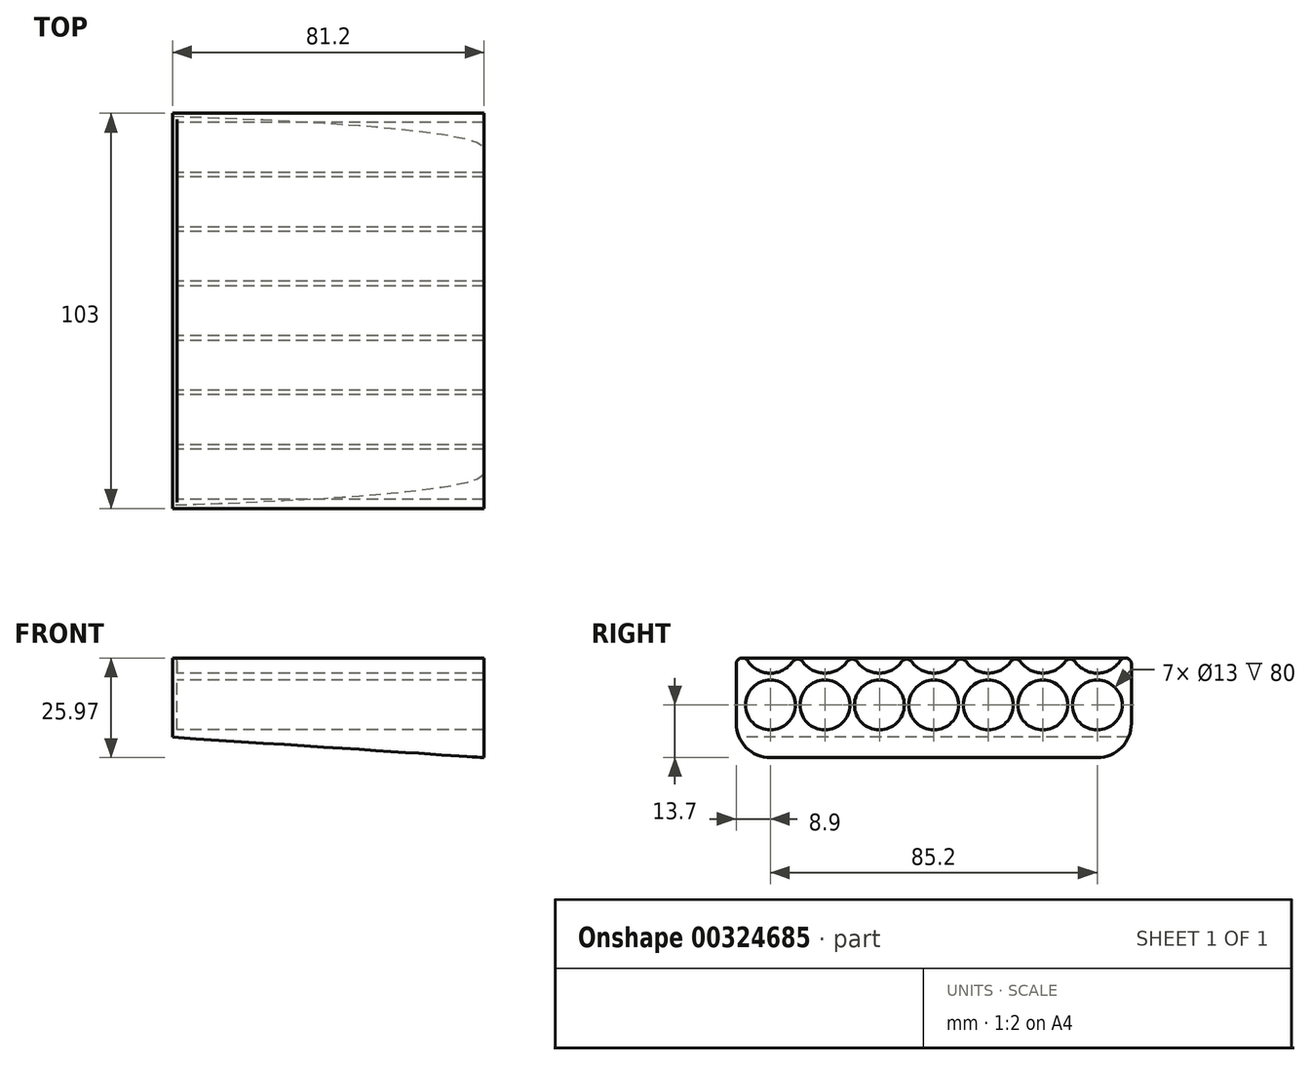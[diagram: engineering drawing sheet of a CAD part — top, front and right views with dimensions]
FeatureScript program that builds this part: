
annotation { "Feature Type Name" : "Feature", "Feature Type Description" : "" }
export const myFeature = defineFeature(function(context is Context, id is Id, definition is map)
    precondition{}
    {
        {
            var Q0;
            Q0=qCreatedBy(makeId("Right.planeOp"),FACE);
            var sketch = newSketch(context, id + "F0", { "sketchPlane" : qUnion([Q0])});
            skCircle(sketch, "E0", {"center": v(0, 0) * mm, "radius": 6.5 * mm});
            skCircle(sketch, "E1.1.0.0", {"center": v(14.2, 0) * mm, "radius": 6.5 * mm});
            skCircle(sketch, "E1.2.0.0", {"center": v(28.4, 0) * mm, "radius": 6.5 * mm});
            skCircle(sketch, "E1.3.0.0", {"center": v(42.6, 0) * mm, "radius": 6.5 * mm});
            skCircle(sketch, "E1.4.0.0", {"center": v(56.8, 0) * mm, "radius": 6.5 * mm});
            skCircle(sketch, "E1.5.0.0", {"center": v(71, 0) * mm, "radius": 6.5 * mm});
            skCircle(sketch, "E1.6.0.0", {"center": v(85.2, 0) * mm, "radius": 6.5 * mm});
            skLineSegment(sketch, "E1.direction1", {"start": v(0, 0) * mm, "end": v(14.2, 0) * mm, "construction": true});
            skLineSegment(sketch, "E2.top", {"start": v(0, -13.7) * mm, "end": v(85.2, -13.7) * mm});
            skLineSegment(sketch, "E2.left", {"start": v(-8.9, 11) * mm, "end": v(-8.9, -4.8) * mm});
            skLineSegment(sketch, "E2.right", {"start": v(94.1, 11) * mm, "end": v(94.1, -4.8) * mm});
            skArc(sketch, "E3", {"start": v(-7.05, 14.58) * mm, "mid": v(0.4, 8.31) * mm, "end": v(7.1, 15.4) * mm});
            skArc(sketch, "E4.1.0.0", {"start": v(7.1, 15.4) * mm, "mid": v(14.2, 8.3) * mm, "end": v(21.3, 15.4) * mm});
            skArc(sketch, "E4.2.0.0", {"start": v(21.3, 15.4) * mm, "mid": v(28.4, 8.3) * mm, "end": v(35.5, 15.4) * mm});
            skArc(sketch, "E4.3.0.0", {"start": v(35.5, 15.4) * mm, "mid": v(42.6, 8.3) * mm, "end": v(49.7, 15.4) * mm});
            skArc(sketch, "E4.4.0.0", {"start": v(49.7, 15.4) * mm, "mid": v(56.8, 8.3) * mm, "end": v(63.9, 15.4) * mm});
            skArc(sketch, "E4.5.0.0", {"start": v(63.9, 15.4) * mm, "mid": v(71, 8.3) * mm, "end": v(78.1, 15.4) * mm});
            skArc(sketch, "E4.6.0.0", {"start": v(78.1, 15.4) * mm, "mid": v(84.8, 8.31) * mm, "end": v(92.25, 14.58) * mm});
            skPoint(sketch, "E5.visualSharp", {"position": v(-8.9, -13.7) * mm});
            skArc(sketch, "E5.filletArc", {"start": v(-8.9, -4.8) * mm, "mid": v(-6.3, -11.1) * mm, "end": v(0, -13.7) * mm});
            skPoint(sketch, "E6.visualSharp", {"position": v(94.1, -13.7) * mm});
            skArc(sketch, "E6.filletArc", {"start": v(85.2, -13.7) * mm, "mid": v(91.5, -11.1) * mm, "end": v(94.1, -4.8) * mm});
            skPoint(sketch, "E7.visualSharp", {"position": v(-8.9, 15.4) * mm});
            skArc(sketch, "E7.filletArc", {"start": v(-7.05, 14.58) * mm, "mid": v(-8.41, 13.02) * mm, "end": v(-8.9, 11) * mm});
            skPoint(sketch, "E8.visualSharp", {"position": v(94.1, 15.4) * mm});
            skArc(sketch, "E8.filletArc", {"start": v(94.1, 11) * mm, "mid": v(93.61, 13.02) * mm, "end": v(92.25, 14.58) * mm});
            skSolve(sketch);
        }
        {
            var Q0;
            Q0 = qSketchRegion(id + "F0", true);
            extrude(context, id + "F1", {"entities" : qUnion([Q0]), "depth" : 80 * mm});
        }
        {
            var Q0;
            Q0=makeQuery(id+"F1.opExtrude","SWEPT_EDGE",EDGE,{"disambiguationData":[OSD([sQuery(id+"F0.wireOp",EDGE,"E4.5.0.0"),sQuery(id+"F0.wireOp",EDGE,"E4.6.0.0")])]});
            var Q1;
            Q1=makeQuery(id+"F1.opExtrude","SWEPT_EDGE",EDGE,{"disambiguationData":[OSD([sQuery(id+"F0.wireOp",EDGE,"E4.4.0.0"),sQuery(id+"F0.wireOp",EDGE,"E4.5.0.0")])]});
            var Q2;
            Q2=makeQuery(id+"F1.opExtrude","SWEPT_EDGE",EDGE,{"disambiguationData":[OSD([sQuery(id+"F0.wireOp",EDGE,"E4.3.0.0"),sQuery(id+"F0.wireOp",EDGE,"E4.4.0.0")])]});
            var Q3;
            Q3=makeQuery(id+"F1.opExtrude","SWEPT_EDGE",EDGE,{"disambiguationData":[OSD([sQuery(id+"F0.wireOp",EDGE,"E4.2.0.0"),sQuery(id+"F0.wireOp",EDGE,"E4.3.0.0")])]});
            var Q4;
            Q4=makeQuery(id+"F1.opExtrude","SWEPT_EDGE",EDGE,{"disambiguationData":[OSD([sQuery(id+"F0.wireOp",EDGE,"E4.1.0.0"),sQuery(id+"F0.wireOp",EDGE,"E4.2.0.0")])]});
            var Q5;
            Q5=makeQuery(id+"F1.opExtrude","SWEPT_EDGE",EDGE,{"disambiguationData":[OSD([sQuery(id+"F0.wireOp",EDGE,"E3"),sQuery(id+"F0.wireOp",EDGE,"E4.1.0.0")])]});
            var Q6;
            Q6=makeQuery(id+"F1.opExtrude","SWEPT_EDGE",EDGE,{"disambiguationData":[OSD([sQuery(id+"F0.wireOp",EDGE,"E4.6.0.0"),sQuery(id+"F0.wireOp",EDGE,"E8.filletArc")])]});
            var Q7;
            Q7=makeQuery(id+"F1.opExtrude","SWEPT_EDGE",EDGE,{"disambiguationData":[OSD([sQuery(id+"F0.wireOp",EDGE,"E3"),sQuery(id+"F0.wireOp",EDGE,"E7.filletArc")])]});
            fillet(context, id + "F2", {"entities" : qUnion([Q0, Q1, Q2, Q3, Q4, Q5, Q6, Q7]), "radius" : 1.6 * mm, "tangentPropagation" : true, "allowEdgeOverflow" : false});
        }
        {
            var Q0;
            Q0=makeQuery(id+"F1.opExtrude","CAP_FACE",FACE,{"disambiguationData":[OSD([sQuery(id+"F0.wireOp",EDGE,"E0"),sQuery(id+"F0.wireOp",EDGE,"E1.1.0.0"),sQuery(id+"F0.wireOp",EDGE,"E1.2.0.0"),sQuery(id+"F0.wireOp",EDGE,"E1.3.0.0"),sQuery(id+"F0.wireOp",EDGE,"E1.4.0.0"),sQuery(id+"F0.wireOp",EDGE,"E1.5.0.0"),sQuery(id+"F0.wireOp",EDGE,"E1.6.0.0"),sQuery(id+"F0.wireOp",EDGE,"E2.top"),sQuery(id+"F0.wireOp",EDGE,"E2.left"),sQuery(id+"F0.wireOp",EDGE,"E2.right"),sQuery(id+"F0.wireOp",EDGE,"E3"),sQuery(id+"F0.wireOp",EDGE,"E4.1.0.0"),sQuery(id+"F0.wireOp",EDGE,"E4.2.0.0"),sQuery(id+"F0.wireOp",EDGE,"E4.3.0.0"),sQuery(id+"F0.wireOp",EDGE,"E4.4.0.0"),sQuery(id+"F0.wireOp",EDGE,"E4.5.0.0"),sQuery(id+"F0.wireOp",EDGE,"E4.6.0.0"),sQuery(id+"F0.wireOp",EDGE,"E5.filletArc"),sQuery(id+"F0.wireOp",EDGE,"E6.filletArc"),sQuery(id+"F0.wireOp",EDGE,"E7.filletArc"),sQuery(id+"F0.wireOp",EDGE,"E8.filletArc")])],"isStart":true});
            var sketch = newSketch(context, id + "F3", { "sketchPlane" : qUnion([Q0])});
            skPoint(sketch, "E9.startSnap0", {"position": v(-92.95, 12.2) * mm});
            skPoint(sketch, "E9.endSnap0", {"position": v(-35.5, 11.97) * mm});
            skLineSegment(sketch, "E10.0", {"start": v(-94.1, 10.67) * mm, "end": v(-94.1, -4.8) * mm});
            skArc(sketch, "E10.1", {"start": v(-85.2, -13.7) * mm, "mid": v(-91.5, -11.1) * mm, "end": v(-94.1, -4.8) * mm});
            skLineSegment(sketch, "E10.2", {"start": v(0, -13.7) * mm, "end": v(-85.2, -13.7) * mm});
            skArc(sketch, "E10.3", {"start": v(8.9, -4.8) * mm, "mid": v(6.3, -11.1) * mm, "end": v(0, -13.7) * mm});
            skLineSegment(sketch, "E10.4", {"start": v(8.9, 10.67) * mm, "end": v(8.9, -4.8) * mm});
            skArc(sketch, "E10.5", {"start": v(8.9, 10.67) * mm, "mid": v(8.43, 11.8) * mm, "end": v(7.3, 12.27) * mm});
            skArc(sketch, "E10.6", {"start": v(-92.5, 12.27) * mm, "mid": v(-93.63, 11.8) * mm, "end": v(-94.1, 10.67) * mm});
            skLineSegment(sketch, "E11", {"start": v(-92.5, 12.27) * mm, "end": v(7.3, 12.27) * mm});
            skPoint(sketch, "E12.orphan", {"position": v(-91.16, 11.54) * mm});
            skPoint(sketch, "E13.orphan", {"position": v(5.96, 11.54) * mm});
            skSolve(sketch);
        }
        {
            var Q0;
            Q0 = qSketchRegion(id + "F3", true);
            extrude(context, id + "F4", {"entities" : qUnion([Q0]), "operationType" : NewBodyOperationType.ADD, "depth" : 1.2 * mm});
        }
        {
            var Q0;
            Q0=qCreatedBy(makeId("Front.planeOp"),FACE);
            var sketch = newSketch(context, id + "F5", { "sketchPlane" : qUnion([Q0])});
            skLineSegment(sketch, "E14", {"start": v(-1.2, -8.4) * mm, "end": v(79.8, -13.7) * mm});
            skLineSegment(sketch, "E15", {"start": v(79.8, -13.7) * mm, "end": v(79.8, -25.43) * mm});
            skLineSegment(sketch, "E16", {"start": v(79.8, -25.43) * mm, "end": v(-2.69, -26.33) * mm});
            skLineSegment(sketch, "E17", {"start": v(-2.69, -26.33) * mm, "end": v(-1.2, -8.4) * mm});
            skSolve(sketch);
        }
        {
            var Q0;
            Q0 = qSketchRegion(id + "F5", true);
            extrude(context, id + "F6", {"entities" : qUnion([Q0]), "operationType" : NewBodyOperationType.REMOVE, "endBound" : BoundingType.SYMMETRIC, "oppositeDirection" : true, "depth" : 200 * mm});
        }
    });
